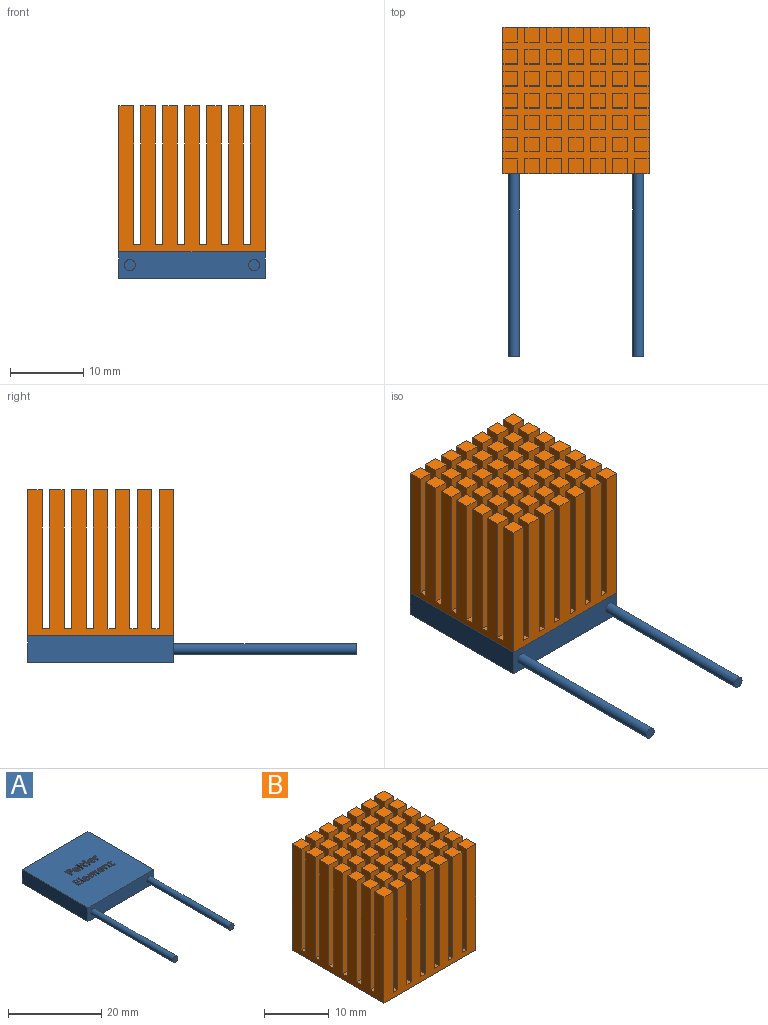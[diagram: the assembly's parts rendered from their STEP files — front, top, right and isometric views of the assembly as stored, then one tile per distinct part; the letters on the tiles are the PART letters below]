
ASSEMBLY  parts=2 mates=1
PART A: 202 faces, bbox 20x45x3.6 mm
  f0: plane 20x20mm, normal (0,0,1), area 381.4mm2, adj f2,f3,f4,f5,f6,f7,f8,f9
  f1: plane 20x20mm, normal (0,0,-1), area 381.4mm2, adj f2,f3,f4,f5,f6,f7,f8,f9
  f2: plane 20x3.6mm, normal (0,1,0), area 72mm2, adj f0,f1,f3,f5
  f3: plane 20x3.6mm, normal (-1,0,0), area 72mm2, adj f0,f1,f2,f4
  f4: plane 20x3.6mm, normal (0,-1,0), area 68.5mm2, adj f0,f1,f3,f5,f198,f200
  f5: plane 20x3.6mm, normal (1,0,0), area 72mm2, adj f0,f1,f2,f4
  f6: plane 3.6x0.41mm, normal (0,1,0), area 1.5mm2, adj f0,f1,f7,f9
  f7: plane 3.6x2.11mm, normal (-1,0,0), area 7.6mm2, adj f0,f1,f6,f8
  f8: plane 3.6x0.41mm, normal (0,-1,0), area 1.5mm2, adj f0,f1,f7,f9
  f9: plane 3.6x2.11mm, normal (1,0,0), area 7.6mm2, adj f0,f1,f6,f8
  f10: extruded ~3.6x0.57mm, area 2.3mm2, adj f0,f1,f11,f24
  f11: extruded ~3.6x0.59mm, area 2.3mm2, adj f0,f1,f10,f12
  f12: extruded ~3.6x0.53mm, area 2.1mm2, adj f0,f1,f11,f13
  f13: extruded ~3.6x0.5mm, area 2mm2, adj f0,f1,f12,f14
  f14: extruded ~3.6x0.51mm, area 2mm2, adj f0,f1,f13,f15
  f15: plane 3.6x0.2mm, normal (-1,0,0), area 0.7mm2, adj f0,f1,f14,f16
  f16: plane 3.6x0.98mm, normal (0,1,0), area 3.5mm2, adj f0,f1,f15,f17
  f17: extruded ~3.6x0.28mm, area 1.1mm2, adj f0,f1,f16,f18
  f18: extruded ~3.6x0.27mm, area 1.1mm2, adj f0,f1,f17,f19
  f19: extruded ~3.6x0.26mm, area 0.9mm2, adj f0,f1,f18,f20
  f20: extruded ~3.6x0.25mm, area 1mm2, adj f0,f1,f19,f21
  f21: plane 3.6x0.32mm, normal (-1,0,0), area 1.2mm2, adj f0,f1,f20,f22
  f22: extruded ~3.6x0.23mm, area 0.9mm2, adj f0,f1,f21,f23
  f23: extruded ~3.6x0.3mm, area 1.1mm2, adj f0,f1,f22,f24
  f24: extruded ~3.6x0.57mm, area 2.2mm2, adj f0,f1,f10,f23
  f25: extruded ~3.6x0.57mm, area 2.3mm2, adj f0,f1,f26,f39
  f26: extruded ~3.6x0.59mm, area 2.3mm2, adj f0,f1,f25,f27
  f27: extruded ~3.6x0.53mm, area 2.1mm2, adj f0,f1,f26,f28
  f28: extruded ~3.6x0.5mm, area 2mm2, adj f0,f1,f27,f29
  f29: extruded ~3.6x0.51mm, area 2mm2, adj f0,f1,f28,f30
  f30: plane 3.6x0.2mm, normal (-1,0,0), area 0.7mm2, adj f0,f1,f29,f31
  f31: plane 3.6x0.98mm, normal (0,1,0), area 3.5mm2, adj f0,f1,f30,f32
  f32: extruded ~3.6x0.28mm, area 1.1mm2, adj f0,f1,f31,f33
  f33: extruded ~3.6x0.27mm, area 1.1mm2, adj f0,f1,f32,f34
  f34: extruded ~3.6x0.26mm, area 0.9mm2, adj f0,f1,f33,f35
  f35: extruded ~3.6x0.25mm, area 1mm2, adj f0,f1,f34,f36
  f36: plane 3.6x0.32mm, normal (-1,0,0), area 1.2mm2, adj f0,f1,f35,f37
  f37: extruded ~3.6x0.23mm, area 0.9mm2, adj f0,f1,f36,f38
  f38: extruded ~3.6x0.3mm, area 1.1mm2, adj f0,f1,f37,f39
  f39: extruded ~3.6x0.57mm, area 2.2mm2, adj f0,f1,f25,f38
  f40: extruded ~3.6x0.57mm, area 2.2mm2, adj f0,f1,f41,f48
  f41: plane 3.6x0.18mm, normal (0,1,0), area 0.6mm2, adj f0,f1,f40,f42
  f42: plane 3.6x0.71mm, normal (-1,0,0), area 2.5mm2, adj f0,f1,f41,f43
  f43: plane 3.6x0.42mm, normal (0,1,0), area 1.5mm2, adj f0,f1,f42,f44
  f44: plane 3.6x1.98mm, normal (1,0,0), area 7.1mm2, adj f0,f1,f43,f45
  f45: plane 3.6x0.63mm, normal (0,-1,0), area 2.3mm2, adj f0,f1,f44,f46
  f46: extruded ~3.6x0.55mm, area 2.1mm2, adj f0,f1,f45,f47
  f47: extruded ~3.6x0.46mm, area 1.9mm2, adj f0,f1,f46,f48
  f48: extruded ~3.6x0.49mm, area 2mm2, adj f0,f1,f40,f47
  f49: extruded ~3.6x0.26mm, area 1mm2, adj f0,f1,f50,f66
  f50: extruded ~3.6x0.13mm, area 0.5mm2, adj f0,f1,f49,f51
  f51: extruded ~3.6x0.13mm, area 0.5mm2, adj f0,f1,f50,f52
  f52: plane 3.6x0.73mm, normal (-1,0,0), area 2.6mm2, adj f0,f1,f51,f53
  f53: plane 3.6x0.42mm, normal (0,1,0), area 1.5mm2, adj f0,f1,f52,f54
  f54: plane 3.6x0.31mm, normal (-1,0,0), area 1.1mm2, adj f0,f1,f53,f55
  f55: plane 3.6x0.42mm, normal (0,-1,0), area 1.5mm2, adj f0,f1,f54,f56
  f56: plane 3.6x0.32mm, normal (-1,0,0), area 1.2mm2, adj f0,f1,f55,f57
  f57: plane 3.6x0.26mm, normal (0,-1,0), area 1mm2, adj f0,f1,f56,f58
  f58: plane 3.6x0.32mm, normal (0.94,-0.35,0), area 1.2mm2, adj f0,f1,f57,f59
  f59: plane 3.6x0.23mm, normal (0.52,-0.85,0), area 1mm2, adj f0,f1,f58,f60
  f60: plane 3.6x0.18mm, normal (1,0,0), area 0.6mm2, adj f0,f1,f59,f61
  f61: plane 3.6x0.2mm, normal (0,1,0), area 0.7mm2, adj f0,f1,f60,f62
  f62: plane 3.6x0.73mm, normal (1,0,0), area 2.6mm2, adj f0,f1,f61,f63
  f63: extruded ~3.6x0.38mm, area 1.4mm2, adj f0,f1,f62,f64
  f64: extruded ~3.6x0.36mm, area 1.4mm2, adj f0,f1,f63,f65
  f65: extruded ~3.6x0.38mm, area 1.4mm2, adj f0,f1,f64,f66
  f66: plane 3.6x0.31mm, normal (-1,0,0), area 1.1mm2, adj f0,f1,f49,f65
  f67: extruded ~3.6x0.57mm, area 2.3mm2, adj f0,f1,f68,f81
  f68: extruded ~3.6x0.59mm, area 2.3mm2, adj f0,f1,f67,f69
  f69: extruded ~3.6x0.53mm, area 2.1mm2, adj f0,f1,f68,f70
  f70: extruded ~3.6x0.5mm, area 2mm2, adj f0,f1,f69,f71
  f71: extruded ~3.6x0.51mm, area 2mm2, adj f0,f1,f70,f72
  f72: plane 3.6x0.2mm, normal (-1,0,0), area 0.7mm2, adj f0,f1,f71,f73
  f73: plane 3.6x0.98mm, normal (0,1,0), area 3.5mm2, adj f0,f1,f72,f74
  f74: extruded ~3.6x0.28mm, area 1.1mm2, adj f0,f1,f73,f75
  f75: extruded ~3.6x0.27mm, area 1.1mm2, adj f0,f1,f74,f76
  f76: extruded ~3.6x0.26mm, area 0.9mm2, adj f0,f1,f75,f77
  f77: extruded ~3.6x0.25mm, area 1mm2, adj f0,f1,f76,f78
  f78: plane 3.6x0.32mm, normal (-1,0,0), area 1.2mm2, adj f0,f1,f77,f79
  f79: extruded ~3.6x0.23mm, area 0.9mm2, adj f0,f1,f78,f80
  f80: extruded ~3.6x0.3mm, area 1.1mm2, adj f0,f1,f79,f81
  f81: extruded ~3.6x0.57mm, area 2.2mm2, adj f0,f1,f67,f80
  f82: extruded ~3.6x0.57mm, area 2.3mm2, adj f0,f1,f83,f96
  f83: extruded ~3.6x0.59mm, area 2.3mm2, adj f0,f1,f82,f84
  f84: extruded ~3.6x0.53mm, area 2.1mm2, adj f0,f1,f83,f85
  f85: extruded ~3.6x0.5mm, area 2mm2, adj f0,f1,f84,f86
  f86: extruded ~3.6x0.51mm, area 2mm2, adj f0,f1,f85,f87
  f87: plane 3.6x0.2mm, normal (-1,0,0), area 0.7mm2, adj f0,f1,f86,f88
  f88: plane 3.6x0.98mm, normal (0,1,0), area 3.5mm2, adj f0,f1,f87,f89
  f89: extruded ~3.6x0.28mm, area 1.1mm2, adj f0,f1,f88,f90
  f90: extruded ~3.6x0.27mm, area 1.1mm2, adj f0,f1,f89,f91
  f91: extruded ~3.6x0.26mm, area 0.9mm2, adj f0,f1,f90,f92
  f92: extruded ~3.6x0.25mm, area 1mm2, adj f0,f1,f91,f93
  f93: plane 3.6x0.32mm, normal (-1,0,0), area 1.2mm2, adj f0,f1,f92,f94
  f94: extruded ~3.6x0.23mm, area 0.9mm2, adj f0,f1,f93,f95
  f95: extruded ~3.6x0.3mm, area 1.1mm2, adj f0,f1,f94,f96
  f96: extruded ~3.6x0.57mm, area 2.2mm2, adj f0,f1,f82,f95
  f97: plane 3.6x0.41mm, normal (0,1,0), area 1.5mm2, adj f0,f1,f98,f113
  f98: plane 3.6x0.99mm, normal (-1,0,0), area 3.6mm2, adj f0,f1,f97,f99
  f99: extruded ~3.6x0.41mm, area 1.6mm2, adj f0,f1,f98,f100
  f100: extruded ~3.6x0.4mm, area 1.6mm2, adj f0,f1,f99,f101
  f101: extruded ~3.6x0.28mm, area 1mm2, adj f0,f1,f100,f102
  f102: extruded ~3.6x0.19mm, area 0.9mm2, adj f0,f1,f101,f103
  f103: plane 3.6x0.02mm, normal (0,-1,0), area 0.1mm2, adj f0,f1,f102,f104
  f104: plane 3.6x0.19mm, normal (-0.96,-0.28,0), area 0.7mm2, adj f0,f1,f103,f105
  f105: plane 3.6x0.32mm, normal (0,-1,0), area 1.1mm2, adj f0,f1,f104,f106
  f106: plane 3.6x1.52mm, normal (1,0,0), area 5.5mm2, adj f0,f1,f105,f107
  f107: plane 3.6x0.41mm, normal (0,1,0), area 1.5mm2, adj f0,f1,f106,f108
  f108: plane 3.6x0.71mm, normal (-1,0,0), area 2.6mm2, adj f0,f1,f107,f109
  f109: extruded ~3.6x0.38mm, area 1.4mm2, adj f0,f1,f108,f110
  f110: extruded ~3.6x0.25mm, area 1mm2, adj f0,f1,f109,f111
  f111: extruded ~3.6x0.19mm, area 0.8mm2, adj f0,f1,f110,f112
  f112: extruded ~3.6x0.25mm, area 0.9mm2, adj f0,f1,f111,f113
  f113: plane 3.6x0.89mm, normal (1,0,0), area 3.2mm2, adj f0,f1,f97,f112
  f114: plane 3.6x0.41mm, normal (0,1,0), area 1.5mm2, adj f0,f1,f115,f141
  f115: plane 3.6x0.76mm, normal (-1,0,0), area 2.7mm2, adj f0,f1,f114,f116
  f116: extruded ~3.6x0.34mm, area 1.3mm2, adj f0,f1,f115,f117
  f117: extruded ~3.6x0.23mm, area 0.9mm2, adj f0,f1,f116,f118
  f118: extruded ~3.6x0.17mm, area 0.7mm2, adj f0,f1,f117,f119
  f119: extruded ~3.6x0.25mm, area 0.9mm2, adj f0,f1,f118,f120
  f120: plane 3.6x0.89mm, normal (1,0,0), area 3.2mm2, adj f0,f1,f119,f121
  f121: plane 3.6x0.42mm, normal (0,1,0), area 1.5mm2, adj f0,f1,f120,f122
  f122: plane 3.6x0.99mm, normal (-1,0,0), area 3.6mm2, adj f0,f1,f121,f123
  f123: extruded ~3.6x0.42mm, area 1.6mm2, adj f0,f1,f122,f124
  f124: extruded ~3.6x0.39mm, area 1.5mm2, adj f0,f1,f123,f125
  f125: extruded ~3.6x0.27mm, area 1mm2, adj f0,f1,f124,f126
  f126: extruded ~3.6x0.18mm, area 0.9mm2, adj f0,f1,f125,f127
  f127: plane 3.6x0.04mm, normal (0,-1,0), area 0.1mm2, adj f0,f1,f126,f128
  f128: extruded ~3.6x0.46mm, area 1.9mm2, adj f0,f1,f127,f129
  f129: extruded ~3.6x0.26mm, area 1mm2, adj f0,f1,f128,f130
  f130: extruded ~3.6x0.18mm, area 0.9mm2, adj f0,f1,f129,f131
  f131: plane 3.6x0.02mm, normal (0,-1,0), area 0.1mm2, adj f0,f1,f130,f132
  f132: plane 3.6x0.19mm, normal (-0.96,-0.28,0), area 0.7mm2, adj f0,f1,f131,f133
  f133: plane 3.6x0.32mm, normal (0,-1,0), area 1.1mm2, adj f0,f1,f132,f134
  f134: plane 3.6x1.52mm, normal (1,0,0), area 5.5mm2, adj f0,f1,f133,f135
  f135: plane 3.6x0.41mm, normal (0,1,0), area 1.5mm2, adj f0,f1,f134,f136
  f136: plane 3.6x0.71mm, normal (-1,0,0), area 2.6mm2, adj f0,f1,f135,f137
  f137: extruded ~3.6x0.38mm, area 1.4mm2, adj f0,f1,f136,f138
  f138: extruded ~3.6x0.23mm, area 1mm2, adj f0,f1,f137,f139
  f139: extruded ~3.6x0.17mm, area 0.7mm2, adj f0,f1,f138,f140
  f140: extruded ~3.6x0.25mm, area 0.9mm2, adj f0,f1,f139,f141
  f141: plane 3.6x0.89mm, normal (1,0,0), area 3.2mm2, adj f0,f1,f114,f140
  f142: plane 3.6x0.41mm, normal (0,1,0), area 1.5mm2, adj f0,f1,f143,f145
  f143: plane 3.6x2.11mm, normal (-1,0,0), area 7.6mm2, adj f0,f1,f142,f144
  f144: plane 3.6x0.41mm, normal (0,-1,0), area 1.5mm2, adj f0,f1,f143,f145
  f145: plane 3.6x2.11mm, normal (1,0,0), area 7.6mm2, adj f0,f1,f142,f144
  f146: plane 3.6x1.14mm, normal (0,1,0), area 4.1mm2, adj f0,f1,f147,f157
  f147: plane 3.6x0.35mm, normal (-1,0,0), area 1.2mm2, adj f0,f1,f146,f148
  f148: plane 3.6x0.72mm, normal (0,-1,0), area 2.6mm2, adj f0,f1,f147,f149
  f149: plane 3.6x0.51mm, normal (-1,0,0), area 1.8mm2, adj f0,f1,f148,f150
  f150: plane 3.6x0.67mm, normal (0,1,0), area 2.4mm2, adj f0,f1,f149,f151
  f151: plane 3.6x0.34mm, normal (-1,0,0), area 1.2mm2, adj f0,f1,f150,f152
  f152: plane 3.6x0.67mm, normal (0,-1,0), area 2.4mm2, adj f0,f1,f151,f153
  f153: plane 3.6x0.44mm, normal (-1,0,0), area 1.6mm2, adj f0,f1,f152,f154
  f154: plane 3.6x0.72mm, normal (0,1,0), area 2.6mm2, adj f0,f1,f153,f155
  f155: plane 3.6x0.34mm, normal (-1,0,0), area 1.2mm2, adj f0,f1,f154,f156
  f156: plane 3.6x1.14mm, normal (0,-1,0), area 4.1mm2, adj f0,f1,f155,f157
  f157: plane 3.6x1.98mm, normal (1,0,0), area 7.1mm2, adj f0,f1,f146,f156
  f158: extruded ~3.6x0.26mm, area 1mm2, adj f0,f1,f159,f175
  f159: extruded ~3.6x0.13mm, area 0.5mm2, adj f0,f1,f158,f160
  f160: extruded ~3.6x0.13mm, area 0.5mm2, adj f0,f1,f159,f161
  f161: plane 3.6x0.73mm, normal (-1,0,0), area 2.6mm2, adj f0,f1,f160,f162
  f162: plane 3.6x0.42mm, normal (0,1,0), area 1.5mm2, adj f0,f1,f161,f163
  f163: plane 3.6x0.31mm, normal (-1,0,0), area 1.1mm2, adj f0,f1,f162,f164
  f164: plane 3.6x0.42mm, normal (0,-1,0), area 1.5mm2, adj f0,f1,f163,f165
  f165: plane 3.6x0.32mm, normal (-1,0,0), area 1.2mm2, adj f0,f1,f164,f166
  f166: plane 3.6x0.26mm, normal (0,-1,0), area 1mm2, adj f0,f1,f165,f167
  f167: plane 3.6x0.32mm, normal (0.94,-0.35,0), area 1.2mm2, adj f0,f1,f166,f168
  f168: plane 3.6x0.23mm, normal (0.52,-0.85,0), area 1mm2, adj f0,f1,f167,f169
  f169: plane 3.6x0.18mm, normal (1,0,0), area 0.6mm2, adj f0,f1,f168,f170
  f170: plane 3.6x0.2mm, normal (0,1,0), area 0.7mm2, adj f0,f1,f169,f171
  f171: plane 3.6x0.73mm, normal (1,0,0), area 2.6mm2, adj f0,f1,f170,f172
  f172: extruded ~3.6x0.38mm, area 1.4mm2, adj f0,f1,f171,f173
  f173: extruded ~3.6x0.36mm, area 1.4mm2, adj f0,f1,f172,f174
  f174: extruded ~3.6x0.38mm, area 1.4mm2, adj f0,f1,f173,f175
  f175: plane 3.6x0.31mm, normal (-1,0,0), area 1.1mm2, adj f0,f1,f158,f174
  f176: extruded ~3.6x0.23mm, area 1.2mm2, adj f0,f1,f177,f180
  f177: extruded ~3.6x0.23mm, area 1.3mm2, adj f0,f1,f176,f178
  f178: extruded ~3.6x0.17mm, area 0.7mm2, adj f0,f1,f177,f179
  f179: extruded ~3.6x0.15mm, area 0.6mm2, adj f0,f1,f178,f180
  f180: extruded ~3.6x0.23mm, area 1.2mm2, adj f0,f1,f176,f179
  f181: plane 3.6x0.41mm, normal (0,1,0), area 1.5mm2, adj f0,f1,f182,f184
  f182: plane 3.6x1.52mm, normal (-1,0,0), area 5.5mm2, adj f0,f1,f181,f183
  f183: plane 3.6x0.41mm, normal (0,-1,0), area 1.5mm2, adj f0,f1,f182,f184
  f184: plane 3.6x1.52mm, normal (1,0,0), area 5.5mm2, adj f0,f1,f181,f183
  f185: extruded ~3.6x0.14mm, area 0.5mm2, adj f0,f1,f186,f197
  f186: extruded ~3.6x0.26mm, area 1mm2, adj f0,f1,f185,f187
  f187: extruded ~3.6x0.21mm, area 1mm2, adj f0,f1,f186,f188
  f188: plane 3.6x0.02mm, normal (0,-1,0), area 0.1mm2, adj f0,f1,f187,f189
  f189: plane 3.6x0.26mm, normal (-0.97,-0.23,0), area 0.9mm2, adj f0,f1,f188,f190
  f190: plane 3.6x0.31mm, normal (0,-1,0), area 1.1mm2, adj f0,f1,f189,f191
  f191: plane 3.6x1.52mm, normal (1,0,0), area 5.5mm2, adj f0,f1,f190,f192
  f192: plane 3.6x0.41mm, normal (0,1,0), area 1.5mm2, adj f0,f1,f191,f193
  f193: plane 3.6x0.77mm, normal (-1,0,0), area 2.8mm2, adj f0,f1,f192,f194
  f194: extruded ~3.6x0.29mm, area 1.1mm2, adj f0,f1,f193,f195
  f195: extruded ~3.6x0.31mm, area 1.2mm2, adj f0,f1,f194,f196
  f196: extruded ~3.6x0.12mm, area 0.4mm2, adj f0,f1,f195,f197
  f197: plane 3.6x0.39mm, normal (-1,0.08,0), area 1.4mm2, adj f0,f1,f185,f196
  f198: cylinder r=0.75mm len=25mm, axis (0,1,0), area 117.8mm2, adj f4,f199
  f199: plane 1.5x1.5mm, normal (0,-1,0), area 1.8mm2, adj f198
  f200: cylinder r=0.75mm len=25mm, axis (0,1,0), area 117.8mm2, adj f4,f201
  f201: plane 1.5x1.5mm, normal (0,-1,0), area 1.8mm2, adj f200
PART B: 223 faces, bbox 20x20x20 mm
  f0: plane 20x20mm, normal (0,0,1), area 204mm2, adj f1,f2,f3,f4,f6,f7,f9,f10
  f1: plane 20x20mm, normal (0,1,0), area 286mm2, adj f0,f2,f4,f5,f7,f8,f29,f30
  f2: plane 20x20mm, normal (-1,0,0), area 286mm2, adj f0,f1,f3,f5,f6,f8,f9,f11
  f3: plane 20x20mm, normal (0,-1,0), area 286mm2, adj f0,f2,f4,f5,f106,f108,f109,f139
  f4: plane 20x20mm, normal (1,0,0), area 286mm2, adj f0,f1,f3,f5,f177,f178,f180,f181
  f5: plane 20x20mm, normal (0,0,-1), area 400mm2, adj f1,f2,f3,f4
  f6: plane 19x2mm, normal (0,-1,0), area 38mm2, adj f0,f2,f7,f8
  f7: plane 19x2mm, normal (1,0,0), area 38mm2, adj f0,f1,f6,f8
  f8: plane 2x2mm, normal (0,0,1), area 4mm2, adj f1,f2,f6,f7
  f9: plane 19x2mm, normal (0,-1,0), area 38mm2, adj f0,f2,f10,f12
  f10: plane 19x2mm, normal (1,0,0), area 38mm2, adj f0,f9,f11,f12
  f11: plane 19x2mm, normal (0,1,0), area 38mm2, adj f0,f2,f10,f12
  f12: plane 2x2mm, normal (0,0,1), area 4mm2, adj f2,f9,f10,f11
  f13: plane 19x2mm, normal (0,-1,0), area 38mm2, adj f0,f2,f14,f16
  f14: plane 19x2mm, normal (1,0,0), area 38mm2, adj f0,f13,f15,f16
  f15: plane 19x2mm, normal (0,1,0), area 38mm2, adj f0,f2,f14,f16
  f16: plane 2x2mm, normal (0,0,1), area 4mm2, adj f2,f13,f14,f15
  f17: plane 19x2mm, normal (0,-1,0), area 38mm2, adj f0,f2,f18,f20
  f18: plane 19x2mm, normal (1,0,0), area 38mm2, adj f0,f17,f19,f20
  f19: plane 19x2mm, normal (0,1,0), area 38mm2, adj f0,f2,f18,f20
  f20: plane 2x2mm, normal (0,0,1), area 4mm2, adj f2,f17,f18,f19
  f21: plane 19x2mm, normal (0,-1,0), area 38mm2, adj f0,f2,f22,f24
  f22: plane 19x2mm, normal (1,0,0), area 38mm2, adj f0,f21,f23,f24
  f23: plane 19x2mm, normal (0,1,0), area 38mm2, adj f0,f2,f22,f24
  f24: plane 2x2mm, normal (0,0,1), area 4mm2, adj f2,f21,f22,f23
  f25: plane 19x2mm, normal (0,-1,0), area 38mm2, adj f0,f2,f26,f28
  f26: plane 19x2mm, normal (1,0,0), area 38mm2, adj f0,f25,f27,f28
  f27: plane 19x2mm, normal (0,1,0), area 38mm2, adj f0,f2,f26,f28
  f28: plane 2x2mm, normal (0,0,1), area 4mm2, adj f2,f25,f26,f27
  f29: plane 19x2mm, normal (1,0,0), area 38mm2, adj f0,f1,f31,f32
  f30: plane 19x2mm, normal (-1,0,0), area 38mm2, adj f0,f1,f31,f32
  f31: plane 19x2mm, normal (0,-1,0), area 38mm2, adj f0,f29,f30,f32
  f32: plane 2x2mm, normal (0,0,1), area 4mm2, adj f1,f29,f30,f31
  f33: plane 19x2mm, normal (-1,0,0), area 38mm2, adj f0,f34,f36,f37
  f34: plane 19x2mm, normal (0,-1,0), area 38mm2, adj f0,f33,f35,f37
  f35: plane 19x2mm, normal (1,0,0), area 38mm2, adj f0,f34,f36,f37
  f36: plane 19x2mm, normal (0,1,0), area 38mm2, adj f0,f33,f35,f37
  f37: plane 2x2mm, normal (0,0,1), area 4mm2, adj f33,f34,f35,f36
  f38: plane 19x2mm, normal (-1,0,0), area 38mm2, adj f0,f39,f41,f42
  f39: plane 19x2mm, normal (0,-1,0), area 38mm2, adj f0,f38,f40,f42
  f40: plane 19x2mm, normal (1,0,0), area 38mm2, adj f0,f39,f41,f42
  f41: plane 19x2mm, normal (0,1,0), area 38mm2, adj f0,f38,f40,f42
  f42: plane 2x2mm, normal (0,0,1), area 4mm2, adj f38,f39,f40,f41
  f43: plane 19x2mm, normal (-1,0,0), area 38mm2, adj f0,f44,f46,f47
  f44: plane 19x2mm, normal (0,-1,0), area 38mm2, adj f0,f43,f45,f47
  f45: plane 19x2mm, normal (1,0,0), area 38mm2, adj f0,f44,f46,f47
  f46: plane 19x2mm, normal (0,1,0), area 38mm2, adj f0,f43,f45,f47
  f47: plane 2x2mm, normal (0,0,1), area 4mm2, adj f43,f44,f45,f46
  f48: plane 19x2mm, normal (-1,0,0), area 38mm2, adj f0,f49,f51,f52
  f49: plane 19x2mm, normal (0,-1,0), area 38mm2, adj f0,f48,f50,f52
  f50: plane 19x2mm, normal (1,0,0), area 38mm2, adj f0,f49,f51,f52
  f51: plane 19x2mm, normal (0,1,0), area 38mm2, adj f0,f48,f50,f52
  f52: plane 2x2mm, normal (0,0,1), area 4mm2, adj f48,f49,f50,f51
  f53: plane 19x2mm, normal (1,0,0), area 38mm2, adj f0,f1,f55,f56
  f54: plane 19x2mm, normal (-1,0,0), area 38mm2, adj f0,f1,f55,f56
  f55: plane 19x2mm, normal (0,-1,0), area 38mm2, adj f0,f53,f54,f56
  f56: plane 2x2mm, normal (0,0,1), area 4mm2, adj f1,f53,f54,f55
  f57: plane 19x2mm, normal (-1,0,0), area 38mm2, adj f0,f58,f60,f61
  f58: plane 19x2mm, normal (0,-1,0), area 38mm2, adj f0,f57,f59,f61
  f59: plane 19x2mm, normal (1,0,0), area 38mm2, adj f0,f58,f60,f61
  f60: plane 19x2mm, normal (0,1,0), area 38mm2, adj f0,f57,f59,f61
  f61: plane 2x2mm, normal (0,0,1), area 4mm2, adj f57,f58,f59,f60
  f62: plane 19x2mm, normal (-1,0,0), area 38mm2, adj f0,f63,f65,f66
  f63: plane 19x2mm, normal (0,-1,0), area 38mm2, adj f0,f62,f64,f66
  f64: plane 19x2mm, normal (1,0,0), area 38mm2, adj f0,f63,f65,f66
  f65: plane 19x2mm, normal (0,1,0), area 38mm2, adj f0,f62,f64,f66
  f66: plane 2x2mm, normal (0,0,1), area 4mm2, adj f62,f63,f64,f65
  f67: plane 19x2mm, normal (-1,0,0), area 38mm2, adj f0,f68,f70,f71
  f68: plane 19x2mm, normal (0,-1,0), area 38mm2, adj f0,f67,f69,f71
  f69: plane 19x2mm, normal (1,0,0), area 38mm2, adj f0,f68,f70,f71
  f70: plane 19x2mm, normal (0,1,0), area 38mm2, adj f0,f67,f69,f71
  f71: plane 2x2mm, normal (0,0,1), area 4mm2, adj f67,f68,f69,f70
  f72: plane 19x2mm, normal (-1,0,0), area 38mm2, adj f0,f73,f75,f76
  f73: plane 19x2mm, normal (0,-1,0), area 38mm2, adj f0,f72,f74,f76
  f74: plane 19x2mm, normal (1,0,0), area 38mm2, adj f0,f73,f75,f76
  f75: plane 19x2mm, normal (0,1,0), area 38mm2, adj f0,f72,f74,f76
  f76: plane 2x2mm, normal (0,0,1), area 4mm2, adj f72,f73,f74,f75
  f77: plane 19x2mm, normal (1,0,0), area 38mm2, adj f0,f1,f79,f80
  f78: plane 19x2mm, normal (-1,0,0), area 38mm2, adj f0,f1,f79,f80
  f79: plane 19x2mm, normal (0,-1,0), area 38mm2, adj f0,f77,f78,f80
  f80: plane 2x2mm, normal (0,0,1), area 4mm2, adj f1,f77,f78,f79
  f81: plane 19x2mm, normal (-1,0,0), area 38mm2, adj f0,f82,f84,f85
  f82: plane 19x2mm, normal (0,-1,0), area 38mm2, adj f0,f81,f83,f85
  f83: plane 19x2mm, normal (1,0,0), area 38mm2, adj f0,f82,f84,f85
  f84: plane 19x2mm, normal (0,1,0), area 38mm2, adj f0,f81,f83,f85
  f85: plane 2x2mm, normal (0,0,1), area 4mm2, adj f81,f82,f83,f84
  f86: plane 19x2mm, normal (-1,0,0), area 38mm2, adj f0,f87,f89,f90
  f87: plane 19x2mm, normal (0,-1,0), area 38mm2, adj f0,f86,f88,f90
  f88: plane 19x2mm, normal (1,0,0), area 38mm2, adj f0,f87,f89,f90
  f89: plane 19x2mm, normal (0,1,0), area 38mm2, adj f0,f86,f88,f90
  f90: plane 2x2mm, normal (0,0,1), area 4mm2, adj f86,f87,f88,f89
  f91: plane 19x2mm, normal (-1,0,0), area 38mm2, adj f0,f92,f94,f95
  f92: plane 19x2mm, normal (0,-1,0), area 38mm2, adj f0,f91,f93,f95
  f93: plane 19x2mm, normal (1,0,0), area 38mm2, adj f0,f92,f94,f95
  f94: plane 19x2mm, normal (0,1,0), area 38mm2, adj f0,f91,f93,f95
  f95: plane 2x2mm, normal (0,0,1), area 4mm2, adj f91,f92,f93,f94
  f96: plane 19x2mm, normal (-1,0,0), area 38mm2, adj f0,f97,f99,f100
  f97: plane 19x2mm, normal (0,-1,0), area 38mm2, adj f0,f96,f98,f100
  f98: plane 19x2mm, normal (1,0,0), area 38mm2, adj f0,f97,f99,f100
  f99: plane 19x2mm, normal (0,1,0), area 38mm2, adj f0,f96,f98,f100
  f100: plane 2x2mm, normal (0,0,1), area 4mm2, adj f96,f97,f98,f99
  f101: plane 19x2mm, normal (-1,0,0), area 38mm2, adj f0,f102,f104,f105
  f102: plane 19x2mm, normal (0,-1,0), area 38mm2, adj f0,f101,f103,f105
  f103: plane 19x2mm, normal (1,0,0), area 38mm2, adj f0,f102,f104,f105
  f104: plane 19x2mm, normal (0,1,0), area 38mm2, adj f0,f101,f103,f105
  f105: plane 2x2mm, normal (0,0,1), area 4mm2, adj f101,f102,f103,f104
  f106: plane 19x2mm, normal (1,0,0), area 38mm2, adj f0,f3,f107,f109
  f107: plane 19x2mm, normal (0,1,0), area 38mm2, adj f0,f106,f108,f109
  f108: plane 19x2mm, normal (-1,0,0), area 38mm2, adj f0,f3,f107,f109
  f109: plane 2x2mm, normal (0,0,1), area 4mm2, adj f3,f106,f107,f108
  f110: plane 19x2mm, normal (1,0,0), area 38mm2, adj f0,f1,f112,f113
  f111: plane 19x2mm, normal (-1,0,0), area 38mm2, adj f0,f1,f112,f113
  f112: plane 19x2mm, normal (0,-1,0), area 38mm2, adj f0,f110,f111,f113
  f113: plane 2x2mm, normal (0,0,1), area 4mm2, adj f1,f110,f111,f112
  f114: plane 19x2mm, normal (-1,0,0), area 38mm2, adj f0,f115,f117,f118
  f115: plane 19x2mm, normal (0,-1,0), area 38mm2, adj f0,f114,f116,f118
  f116: plane 19x2mm, normal (1,0,0), area 38mm2, adj f0,f115,f117,f118
  f117: plane 19x2mm, normal (0,1,0), area 38mm2, adj f0,f114,f116,f118
  f118: plane 2x2mm, normal (0,0,1), area 4mm2, adj f114,f115,f116,f117
  f119: plane 19x2mm, normal (-1,0,0), area 38mm2, adj f0,f120,f122,f123
  f120: plane 19x2mm, normal (0,-1,0), area 38mm2, adj f0,f119,f121,f123
  f121: plane 19x2mm, normal (1,0,0), area 38mm2, adj f0,f120,f122,f123
  f122: plane 19x2mm, normal (0,1,0), area 38mm2, adj f0,f119,f121,f123
  f123: plane 2x2mm, normal (0,0,1), area 4mm2, adj f119,f120,f121,f122
  f124: plane 19x2mm, normal (-1,0,0), area 38mm2, adj f0,f125,f127,f128
  f125: plane 19x2mm, normal (0,-1,0), area 38mm2, adj f0,f124,f126,f128
  f126: plane 19x2mm, normal (1,0,0), area 38mm2, adj f0,f125,f127,f128
  f127: plane 19x2mm, normal (0,1,0), area 38mm2, adj f0,f124,f126,f128
  f128: plane 2x2mm, normal (0,0,1), area 4mm2, adj f124,f125,f126,f127
  f129: plane 19x2mm, normal (-1,0,0), area 38mm2, adj f0,f130,f132,f133
  f130: plane 19x2mm, normal (0,-1,0), area 38mm2, adj f0,f129,f131,f133
  f131: plane 19x2mm, normal (1,0,0), area 38mm2, adj f0,f130,f132,f133
  f132: plane 19x2mm, normal (0,1,0), area 38mm2, adj f0,f129,f131,f133
  f133: plane 2x2mm, normal (0,0,1), area 4mm2, adj f129,f130,f131,f132
  f134: plane 19x2mm, normal (-1,0,0), area 38mm2, adj f0,f135,f137,f138
  f135: plane 19x2mm, normal (0,-1,0), area 38mm2, adj f0,f134,f136,f138
  f136: plane 19x2mm, normal (1,0,0), area 38mm2, adj f0,f135,f137,f138
  f137: plane 19x2mm, normal (0,1,0), area 38mm2, adj f0,f134,f136,f138
  f138: plane 2x2mm, normal (0,0,1), area 4mm2, adj f134,f135,f136,f137
  f139: plane 19x2mm, normal (1,0,0), area 38mm2, adj f0,f3,f140,f142
  f140: plane 19x2mm, normal (0,1,0), area 38mm2, adj f0,f139,f141,f142
  f141: plane 19x2mm, normal (-1,0,0), area 38mm2, adj f0,f3,f140,f142
  f142: plane 2x2mm, normal (0,0,1), area 4mm2, adj f3,f139,f140,f141
  f143: plane 19x2mm, normal (1,0,0), area 38mm2, adj f0,f1,f145,f146
  f144: plane 19x2mm, normal (-1,0,0), area 38mm2, adj f0,f1,f145,f146
  f145: plane 19x2mm, normal (0,-1,0), area 38mm2, adj f0,f143,f144,f146
  f146: plane 2x2mm, normal (0,0,1), area 4mm2, adj f1,f143,f144,f145
  f147: plane 19x2mm, normal (-1,0,0), area 38mm2, adj f0,f148,f150,f151
  f148: plane 19x2mm, normal (0,-1,0), area 38mm2, adj f0,f147,f149,f151
  f149: plane 19x2mm, normal (1,0,0), area 38mm2, adj f0,f148,f150,f151
  f150: plane 19x2mm, normal (0,1,0), area 38mm2, adj f0,f147,f149,f151
  f151: plane 2x2mm, normal (0,0,1), area 4mm2, adj f147,f148,f149,f150
  f152: plane 19x2mm, normal (-1,0,0), area 38mm2, adj f0,f153,f155,f156
  f153: plane 19x2mm, normal (0,-1,0), area 38mm2, adj f0,f152,f154,f156
  f154: plane 19x2mm, normal (1,0,0), area 38mm2, adj f0,f153,f155,f156
  f155: plane 19x2mm, normal (0,1,0), area 38mm2, adj f0,f152,f154,f156
  f156: plane 2x2mm, normal (0,0,1), area 4mm2, adj f152,f153,f154,f155
  f157: plane 19x2mm, normal (-1,0,0), area 38mm2, adj f0,f158,f160,f161
  f158: plane 19x2mm, normal (0,-1,0), area 38mm2, adj f0,f157,f159,f161
  f159: plane 19x2mm, normal (1,0,0), area 38mm2, adj f0,f158,f160,f161
  f160: plane 19x2mm, normal (0,1,0), area 38mm2, adj f0,f157,f159,f161
  f161: plane 2x2mm, normal (0,0,1), area 4mm2, adj f157,f158,f159,f160
  f162: plane 19x2mm, normal (-1,0,0), area 38mm2, adj f0,f163,f165,f166
  f163: plane 19x2mm, normal (0,-1,0), area 38mm2, adj f0,f162,f164,f166
  f164: plane 19x2mm, normal (1,0,0), area 38mm2, adj f0,f163,f165,f166
  f165: plane 19x2mm, normal (0,1,0), area 38mm2, adj f0,f162,f164,f166
  f166: plane 2x2mm, normal (0,0,1), area 4mm2, adj f162,f163,f164,f165
  f167: plane 19x2mm, normal (-1,0,0), area 38mm2, adj f0,f168,f170,f171
  f168: plane 19x2mm, normal (0,-1,0), area 38mm2, adj f0,f167,f169,f171
  f169: plane 19x2mm, normal (1,0,0), area 38mm2, adj f0,f168,f170,f171
  f170: plane 19x2mm, normal (0,1,0), area 38mm2, adj f0,f167,f169,f171
  f171: plane 2x2mm, normal (0,0,1), area 4mm2, adj f167,f168,f169,f170
  f172: plane 19x2mm, normal (1,0,0), area 38mm2, adj f0,f3,f173,f175
  f173: plane 19x2mm, normal (0,1,0), area 38mm2, adj f0,f172,f174,f175
  f174: plane 19x2mm, normal (-1,0,0), area 38mm2, adj f0,f3,f173,f175
  f175: plane 2x2mm, normal (0,0,1), area 4mm2, adj f3,f172,f173,f174
  f176: plane 19x2mm, normal (-1,0,0), area 38mm2, adj f0,f1,f177,f178
  f177: plane 19x2mm, normal (0,-1,0), area 38mm2, adj f0,f4,f176,f178
  f178: plane 2x2mm, normal (0,0,1), area 4mm2, adj f1,f4,f176,f177
  f179: plane 19x2mm, normal (-1,0,0), area 38mm2, adj f0,f180,f181,f182
  f180: plane 19x2mm, normal (0,-1,0), area 38mm2, adj f0,f4,f179,f182
  f181: plane 19x2mm, normal (0,1,0), area 38mm2, adj f0,f4,f179,f182
  f182: plane 2x2mm, normal (0,0,1), area 4mm2, adj f4,f179,f180,f181
  f183: plane 19x2mm, normal (-1,0,0), area 38mm2, adj f0,f184,f185,f186
  f184: plane 19x2mm, normal (0,-1,0), area 38mm2, adj f0,f4,f183,f186
  f185: plane 19x2mm, normal (0,1,0), area 38mm2, adj f0,f4,f183,f186
  f186: plane 2x2mm, normal (0,0,1), area 4mm2, adj f4,f183,f184,f185
  f187: plane 19x2mm, normal (-1,0,0), area 38mm2, adj f0,f188,f189,f190
  f188: plane 19x2mm, normal (0,-1,0), area 38mm2, adj f0,f4,f187,f190
  f189: plane 19x2mm, normal (0,1,0), area 38mm2, adj f0,f4,f187,f190
  f190: plane 2x2mm, normal (0,0,1), area 4mm2, adj f4,f187,f188,f189
  f191: plane 19x2mm, normal (-1,0,0), area 38mm2, adj f0,f192,f193,f194
  f192: plane 19x2mm, normal (0,-1,0), area 38mm2, adj f0,f4,f191,f194
  f193: plane 19x2mm, normal (0,1,0), area 38mm2, adj f0,f4,f191,f194
  f194: plane 2x2mm, normal (0,0,1), area 4mm2, adj f4,f191,f192,f193
  f195: plane 19x2mm, normal (-1,0,0), area 38mm2, adj f0,f196,f197,f198
  f196: plane 19x2mm, normal (0,-1,0), area 38mm2, adj f0,f4,f195,f198
  f197: plane 19x2mm, normal (0,1,0), area 38mm2, adj f0,f4,f195,f198
  f198: plane 2x2mm, normal (0,0,1), area 4mm2, adj f4,f195,f196,f197
  f199: plane 19x2mm, normal (0,1,0), area 38mm2, adj f0,f4,f200,f201
  f200: plane 19x2mm, normal (-1,0,0), area 38mm2, adj f0,f3,f199,f201
  f201: plane 2x2mm, normal (0,0,1), area 4mm2, adj f3,f4,f199,f200
  f202: plane 19x2mm, normal (1,0,0), area 38mm2, adj f0,f3,f203,f204
  f203: plane 19x2mm, normal (0,1,0), area 38mm2, adj f0,f2,f202,f204
  f204: plane 2x2mm, normal (0,0,1), area 4mm2, adj f2,f3,f202,f203
  f205: plane 19x2mm, normal (-1,0,0), area 38mm2, adj f0,f206,f208,f209
  f206: plane 19x2mm, normal (0,-1,0), area 38mm2, adj f0,f205,f207,f209
  f207: plane 19x2mm, normal (1,0,0), area 38mm2, adj f0,f206,f208,f209
  f208: plane 19x2mm, normal (0,1,0), area 38mm2, adj f0,f205,f207,f209
  f209: plane 2x2mm, normal (0,0,1), area 4mm2, adj f205,f206,f207,f208
  f210: plane 19x2mm, normal (1,0,0), area 38mm2, adj f0,f3,f211,f213
  f211: plane 19x2mm, normal (0,1,0), area 38mm2, adj f0,f210,f212,f213
  f212: plane 19x2mm, normal (-1,0,0), area 38mm2, adj f0,f3,f211,f213
  f213: plane 2x2mm, normal (0,0,1), area 4mm2, adj f3,f210,f211,f212
  f214: plane 19x2mm, normal (-1,0,0), area 38mm2, adj f0,f215,f217,f218
  f215: plane 19x2mm, normal (0,-1,0), area 38mm2, adj f0,f214,f216,f218
  f216: plane 19x2mm, normal (1,0,0), area 38mm2, adj f0,f215,f217,f218
  f217: plane 19x2mm, normal (0,1,0), area 38mm2, adj f0,f214,f216,f218
  f218: plane 2x2mm, normal (0,0,1), area 4mm2, adj f214,f215,f216,f217
  f219: plane 19x2mm, normal (1,0,0), area 38mm2, adj f0,f3,f220,f222
  f220: plane 19x2mm, normal (0,1,0), area 38mm2, adj f0,f219,f221,f222
  f221: plane 19x2mm, normal (-1,0,0), area 38mm2, adj f0,f3,f220,f222
  f222: plane 2x2mm, normal (0,0,1), area 4mm2, adj f3,f219,f220,f221
PLACE A rot(axis=(0,1,0),180deg) t=(0,0,0)mm
PLACE B at identity
MATE fastened A.f1 <-> B.f5  axis (0,0,1) through (-10,10,0)mm
